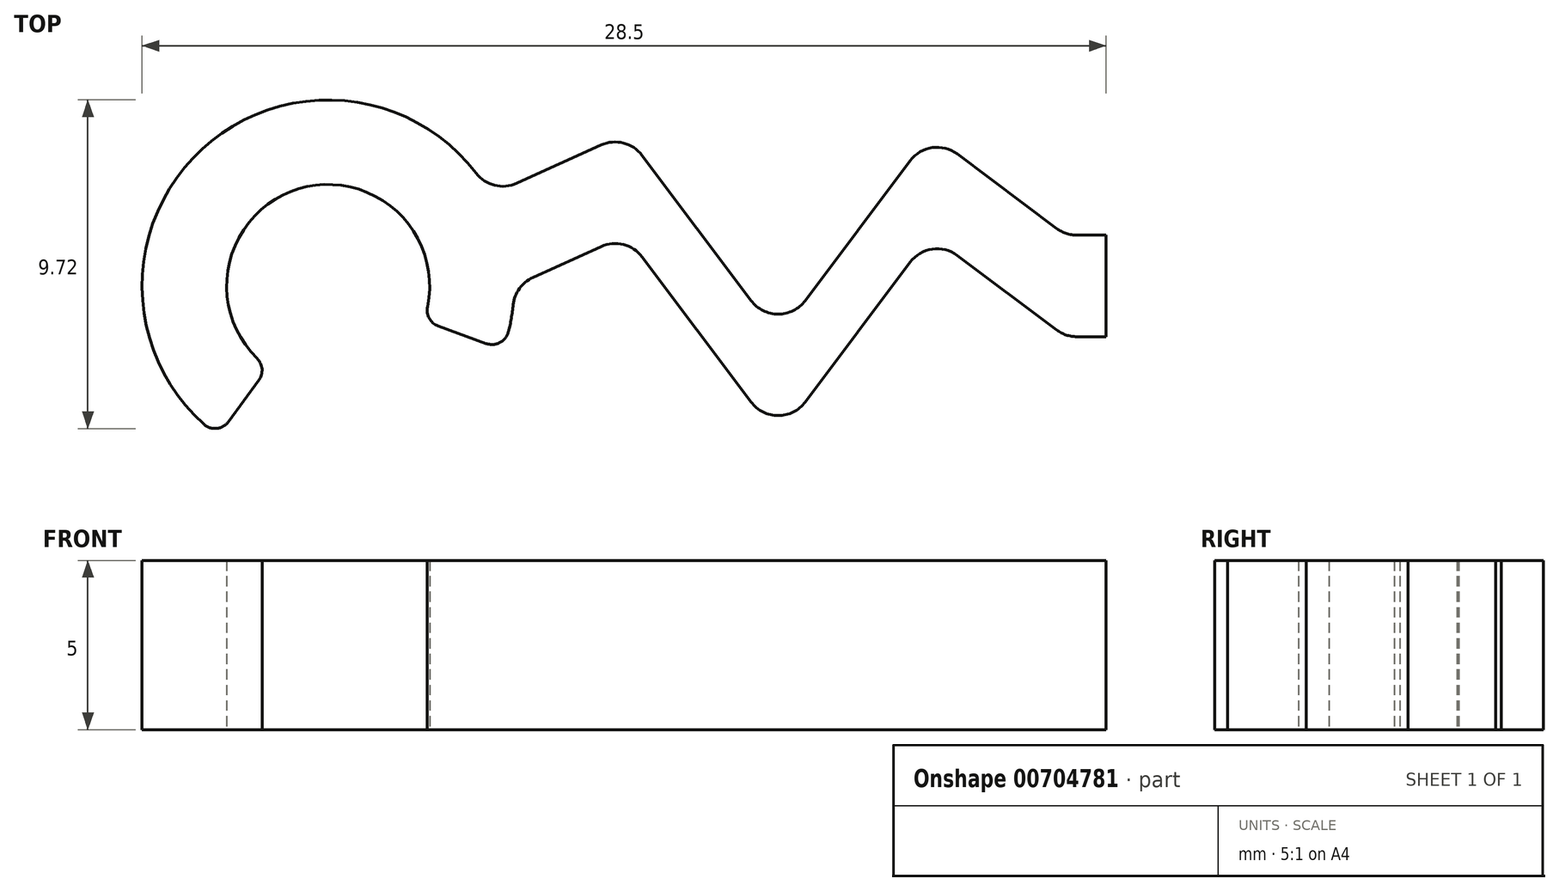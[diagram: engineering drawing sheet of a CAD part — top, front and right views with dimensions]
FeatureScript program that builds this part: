
annotation { "Feature Type Name" : "Feature", "Feature Type Description" : "" }
export const myFeature = defineFeature(function(context is Context, id is Id, definition is map)
    precondition{}
    {
        {
            var Q0;
            Q0=qCreatedBy(makeId("Top.planeOp"),FACE);
            var sketch = newSketch(context, id + "F0", { "sketchPlane" : qUnion([Q0])});
            skArc(sketch, "E0", {"start": v(-20.06, -0.61) * mm, "mid": v(-23.87, 2.87) * mm, "end": v(-25.1, -2.14) * mm});
            skArc(sketch, "E1.0", {"start": v(-17.67, -1.35) * mm, "mid": v(-17.58, -0.96) * mm, "end": v(-17.53, -0.56) * mm});
            skPoint(sketch, "E2", {"position": v(-26, 0) * mm});
            skLineSegment(sketch, "E3", {"start": v(-23, 0) * mm, "end": v(-17.83, -1.88) * mm, "construction": true});
            skLineSegment(sketch, "E4", {"start": v(-23, 0) * mm, "end": v(-26.25, -4.43) * mm, "construction": true});
            skPoint(sketch, "E5", {"position": v(-24.77, -2.42) * mm});
            skPoint(sketch, "E6", {"position": v(-20.18, -1.03) * mm});
            skLineSegment(sketch, "E7", {"start": v(-24.77, -2.42) * mm, "end": v(-20.18, -1.03) * mm, "construction": true});
            skLineSegment(sketch, "E8", {"start": v(-25.05, -2.8) * mm, "end": v(-25.94, -4.01) * mm});
            skLineSegment(sketch, "E9", {"start": v(-19.74, -1.18) * mm, "end": v(-18.33, -1.7) * mm});
            skArc(sketch, "E10.filletArc", {"start": v(-20.06, -0.61) * mm, "mid": v(-20.01, -0.96) * mm, "end": v(-19.74, -1.18) * mm});
            skPoint(sketch, "E11.visualSharp", {"position": v(-17.83, -1.88) * mm});
            skArc(sketch, "E11.filletArc", {"start": v(-18.33, -1.7) * mm, "mid": v(-17.92, -1.67) * mm, "end": v(-17.67, -1.35) * mm});
            skArc(sketch, "E12.filletArc", {"start": v(-25.05, -2.8) * mm, "mid": v(-24.95, -2.46) * mm, "end": v(-25.1, -2.14) * mm});
            skPoint(sketch, "E13.visualSharp", {"position": v(-26.25, -4.43) * mm});
            skArc(sketch, "E13.filletArc", {"start": v(-26.68, -4.09) * mm, "mid": v(-26.3, -4.21) * mm, "end": v(-25.94, -4.01) * mm});
            skLineSegment(sketch, "E14", {"start": v(-26.16, 4.5) * mm, "end": v(0, 4.5) * mm, "construction": true});
            skLineSegment(sketch, "E15.MirrorCS", {"start": v(-26.16, -4.5) * mm, "end": v(0, -4.5) * mm, "construction": true});
            skLineSegment(sketch, "E16", {"start": v(0, 1.5) * mm, "end": v(-26.16, 1.5) * mm, "construction": true});
            skLineSegment(sketch, "E17.MirrorCS", {"start": v(0, -1.5) * mm, "end": v(-26.16, -1.5) * mm, "construction": true});
            skLineSegment(sketch, "E18", {"start": v(-17.42, 3.04) * mm, "end": v(-14.93, 4.17) * mm});
            skLineSegment(sketch, "E19", {"start": v(-13.72, 3.86) * mm, "end": v(-10.5, -0.43) * mm});
            skLineSegment(sketch, "E20", {"start": v(-8.9, -0.43) * mm, "end": v(-5.8, 3.7) * mm});
            skLineSegment(sketch, "E21", {"start": v(-4.4, 3.9) * mm, "end": v(-1.47, 1.7) * mm});
            skLineSegment(sketch, "E22", {"start": v(-1.47, -1.3) * mm, "end": v(-4.4, 0.9) * mm});
            skLineSegment(sketch, "E23", {"start": v(-5.8, 0.7) * mm, "end": v(-8.9, -3.43) * mm});
            skLineSegment(sketch, "E24", {"start": v(-10.5, -3.43) * mm, "end": v(-13.72, 0.86) * mm});
            skLineSegment(sketch, "E25", {"start": v(-14.93, 1.17) * mm, "end": v(-16.95, 0.25) * mm});
            skLineSegment(sketch, "E26", {"start": v(-14.2, 4.5) * mm, "end": v(-14.2, 1.5) * mm, "construction": true});
            skLineSegment(sketch, "E27", {"start": v(-5.2, 1.5) * mm, "end": v(-5.2, 4.5) * mm, "construction": true});
            skLineSegment(sketch, "E28", {"start": v(-9.7, -1.5) * mm, "end": v(-9.7, -4.5) * mm, "construction": true});
            skLineSegment(sketch, "E29", {"start": v(-0.87, 1.5) * mm, "end": v(0, 1.5) * mm});
            skLineSegment(sketch, "E30", {"start": v(0, 1.5) * mm, "end": v(0, -1.5) * mm});
            skLineSegment(sketch, "E31", {"start": v(0, -1.5) * mm, "end": v(-0.87, -1.5) * mm});
            skPoint(sketch, "E32.visualSharp", {"position": v(-14.2, 4.5) * mm});
            skArc(sketch, "E32.filletArc", {"start": v(-13.72, 3.86) * mm, "mid": v(-14.27, 4.23) * mm, "end": v(-14.93, 4.17) * mm});
            skPoint(sketch, "E33.visualSharp", {"position": v(-14.2, 1.5) * mm});
            skArc(sketch, "E33.filletArc", {"start": v(-13.72, 0.86) * mm, "mid": v(-14.27, 1.23) * mm, "end": v(-14.93, 1.17) * mm});
            skPoint(sketch, "E34.visualSharp", {"position": v(-9.7, -4.5) * mm});
            skArc(sketch, "E34.filletArc", {"start": v(-10.5, -3.43) * mm, "mid": v(-9.7, -3.83) * mm, "end": v(-8.9, -3.43) * mm});
            skPoint(sketch, "E35.visualSharp", {"position": v(-9.7, -1.5) * mm});
            skArc(sketch, "E35.filletArc", {"start": v(-10.5, -0.43) * mm, "mid": v(-9.7, -0.83) * mm, "end": v(-8.9, -0.43) * mm});
            skPoint(sketch, "E36.visualSharp", {"position": v(-5.2, 4.5) * mm});
            skArc(sketch, "E36.filletArc", {"start": v(-4.4, 3.9) * mm, "mid": v(-5.14, 4.09) * mm, "end": v(-5.8, 3.7) * mm});
            skPoint(sketch, "E37.visualSharp", {"position": v(-5.2, 1.5) * mm});
            skArc(sketch, "E37.filletArc", {"start": v(-4.4, 0.9) * mm, "mid": v(-5.14, 1.09) * mm, "end": v(-5.8, 0.7) * mm});
            skArc(sketch, "E38.trimOffspring", {"start": v(-18.63, 3.34) * mm, "mid": v(-26.73, 4.04) * mm, "end": v(-26.68, -4.09) * mm});
            skPoint(sketch, "E39.visualSharp", {"position": v(-1.2, 1.5) * mm});
            skArc(sketch, "E39.filletArc", {"start": v(-1.47, 1.7) * mm, "mid": v(-1.18, 1.55) * mm, "end": v(-0.87, 1.5) * mm});
            skPoint(sketch, "E40.visualSharp", {"position": v(-1.2, -1.5) * mm});
            skArc(sketch, "E40.filletArc", {"start": v(-1.47, -1.3) * mm, "mid": v(-1.18, -1.45) * mm, "end": v(-0.87, -1.5) * mm});
            skPoint(sketch, "E41.visualSharp", {"position": v(-18.2, 2.68) * mm});
            skArc(sketch, "E41.filletArc", {"start": v(-18.63, 3.34) * mm, "mid": v(-18.08, 2.98) * mm, "end": v(-17.42, 3.04) * mm});
            skPoint(sketch, "E42.visualSharp", {"position": v(-17.5, 0) * mm});
            skArc(sketch, "E42.filletArc", {"start": v(-16.95, 0.25) * mm, "mid": v(-17.35, -0.08) * mm, "end": v(-17.53, -0.56) * mm});
            skArc(sketch, "E43.MirrorCS", {"start": v(20.06, -0.61) * mm, "mid": v(20.01, -0.96) * mm, "end": v(19.74, -1.18) * mm});
            skArc(sketch, "E44.MirrorCS", {"start": v(25.05, -2.8) * mm, "mid": v(24.95, -2.46) * mm, "end": v(25.1, -2.14) * mm});
            skArc(sketch, "E45.MirrorCS", {"start": v(17.67, -1.35) * mm, "mid": v(17.58, -0.96) * mm, "end": v(17.53, -0.56) * mm});
            skArc(sketch, "E46.MirrorCS", {"start": v(1.47, -1.3) * mm, "mid": v(1.18, -1.45) * mm, "end": v(0.87, -1.5) * mm});
            skArc(sketch, "E47.MirrorCS", {"start": v(13.72, 0.86) * mm, "mid": v(14.27, 1.23) * mm, "end": v(14.93, 1.17) * mm});
            skArc(sketch, "E48.MirrorCS", {"start": v(4.4, 3.9) * mm, "mid": v(5.14, 4.09) * mm, "end": v(5.8, 3.7) * mm});
            skArc(sketch, "E49.MirrorCS", {"start": v(18.33, -1.7) * mm, "mid": v(17.92, -1.67) * mm, "end": v(17.67, -1.35) * mm});
            skArc(sketch, "E50.MirrorCS", {"start": v(1.47, 1.7) * mm, "mid": v(1.18, 1.55) * mm, "end": v(0.87, 1.5) * mm});
            skArc(sketch, "E51.MirrorCS", {"start": v(13.72, 3.86) * mm, "mid": v(14.27, 4.23) * mm, "end": v(14.93, 4.17) * mm});
            skArc(sketch, "E52.MirrorCS", {"start": v(16.95, 0.25) * mm, "mid": v(17.35, -0.08) * mm, "end": v(17.53, -0.56) * mm});
            skArc(sketch, "E53.MirrorCS", {"start": v(26.68, -4.09) * mm, "mid": v(26.3, -4.21) * mm, "end": v(25.94, -4.01) * mm});
            skArc(sketch, "E54.MirrorCS", {"start": v(4.4, 0.9) * mm, "mid": v(5.14, 1.09) * mm, "end": v(5.8, 0.7) * mm});
            skArc(sketch, "E55.MirrorCS", {"start": v(18.63, 3.34) * mm, "mid": v(18.08, 2.98) * mm, "end": v(17.42, 3.04) * mm});
            skPoint(sketch, "E56.MirrorP", {"position": v(24.77, -2.42) * mm});
            skLineSegment(sketch, "E57.MirrorCS", {"start": v(0.87, 1.5) * mm, "end": v(0, 1.5) * mm});
            skLineSegment(sketch, "E58.MirrorCS", {"start": v(0, -1.5) * mm, "end": v(0.87, -1.5) * mm});
            skLineSegment(sketch, "E59.MirrorCS", {"start": v(25.05, -2.8) * mm, "end": v(25.94, -4.01) * mm});
            skPoint(sketch, "E60.MirrorP", {"position": v(20.18, -1.03) * mm});
            skLineSegment(sketch, "E61.MirrorCS", {"start": v(19.74, -1.18) * mm, "end": v(18.33, -1.7) * mm});
            skPoint(sketch, "E62.MirrorP", {"position": v(9.7, -1.5) * mm});
            skLineSegment(sketch, "E63.MirrorCS", {"start": v(4.4, 3.9) * mm, "end": v(1.47, 1.7) * mm});
            skArc(sketch, "E64.MirrorCS", {"start": v(10.5, -3.43) * mm, "mid": v(9.7, -3.83) * mm, "end": v(8.9, -3.43) * mm});
            skLineSegment(sketch, "E65.MirrorCS", {"start": v(1.47, -1.3) * mm, "end": v(4.4, 0.9) * mm});
            skLineSegment(sketch, "E66.MirrorCS", {"start": v(0, -1.5) * mm, "end": v(26.16, -1.5) * mm, "construction": true});
            skLineSegment(sketch, "E67.MirrorCS", {"start": v(17.42, 3.04) * mm, "end": v(14.93, 4.17) * mm});
            skPoint(sketch, "E68.MirrorP", {"position": v(1.2, 1.5) * mm});
            skLineSegment(sketch, "E69.MirrorCS", {"start": v(9.7, -1.5) * mm, "end": v(9.7, -4.5) * mm, "construction": true});
            skArc(sketch, "E70.MirrorCS", {"start": v(20.06, -0.61) * mm, "mid": v(23.87, 2.87) * mm, "end": v(25.1, -2.14) * mm});
            skPoint(sketch, "E71.MirrorP", {"position": v(26, 0) * mm});
            skLineSegment(sketch, "E72.MirrorCS", {"start": v(23, 0) * mm, "end": v(17.83, -1.88) * mm, "construction": true});
            skPoint(sketch, "E73.MirrorP", {"position": v(14.2, 1.5) * mm});
            skLineSegment(sketch, "E74.MirrorCS", {"start": v(5.8, 0.7) * mm, "end": v(8.9, -3.43) * mm});
            skPoint(sketch, "E75.MirrorP", {"position": v(1.2, -1.5) * mm});
            skLineSegment(sketch, "E76.MirrorCS", {"start": v(5.2, 1.5) * mm, "end": v(5.2, 4.5) * mm, "construction": true});
            skLineSegment(sketch, "E77.MirrorCS", {"start": v(10.5, -3.43) * mm, "end": v(13.72, 0.86) * mm});
            skPoint(sketch, "E78.MirrorP", {"position": v(9.7, -4.5) * mm});
            skPoint(sketch, "E79.MirrorP", {"position": v(17.5, 0) * mm});
            skPoint(sketch, "E80.MirrorP", {"position": v(26.25, -4.43) * mm});
            skLineSegment(sketch, "E81.MirrorCS", {"start": v(24.77, -2.42) * mm, "end": v(20.18, -1.03) * mm, "construction": true});
            skLineSegment(sketch, "E82.MirrorCS", {"start": v(13.72, 3.86) * mm, "end": v(10.5, -0.43) * mm});
            skLineSegment(sketch, "E83.MirrorCS", {"start": v(23, 0) * mm, "end": v(26.25, -4.43) * mm, "construction": true});
            skPoint(sketch, "E84.MirrorP", {"position": v(17.83, -1.88) * mm});
            skPoint(sketch, "E85.MirrorP", {"position": v(5.2, 1.5) * mm});
            skPoint(sketch, "E86.MirrorP", {"position": v(18.2, 2.68) * mm});
            skArc(sketch, "E87.MirrorCS", {"start": v(10.5, -0.43) * mm, "mid": v(9.7, -0.83) * mm, "end": v(8.9, -0.43) * mm});
            skArc(sketch, "E88.MirrorCS", {"start": v(18.63, 3.34) * mm, "mid": v(26.73, 4.04) * mm, "end": v(26.68, -4.09) * mm});
            skLineSegment(sketch, "E89.MirrorCS", {"start": v(0, 1.5) * mm, "end": v(26.16, 1.5) * mm, "construction": true});
            skLineSegment(sketch, "E90.MirrorCS", {"start": v(26.16, 4.5) * mm, "end": v(0, 4.5) * mm, "construction": true});
            skPoint(sketch, "E91.MirrorP", {"position": v(5.2, 4.5) * mm});
            skLineSegment(sketch, "E92.MirrorCS", {"start": v(14.93, 1.17) * mm, "end": v(16.95, 0.25) * mm});
            skLineSegment(sketch, "E93.MirrorCS", {"start": v(14.2, 4.5) * mm, "end": v(14.2, 1.5) * mm, "construction": true});
            skPoint(sketch, "E94.MirrorP", {"position": v(14.2, 4.5) * mm});
            skLineSegment(sketch, "E95.MirrorCS", {"start": v(8.9, -0.43) * mm, "end": v(5.8, 3.7) * mm});
            skLineSegment(sketch, "E96.MirrorCS", {"start": v(26.16, -4.5) * mm, "end": v(0, -4.5) * mm, "construction": true});
            skSolve(sketch);
        }
        {
            var Q0;
            Q0=makeQuery(id+"F0.imprint","IMPRINT",FACE,{"disambiguationData":[TD([[makeQuery(id+"F0.imprint","IMPRINT",EDGE,{"derivedFrom":sQuery(id+"F0.wireOp",EDGE,"E0")}),-1.0]])]});
            var Q1;
            Q1=makeQuery(id+"F0.imprint","IMPRINT",FACE,{"disambiguationData":[TD([[makeQuery(id+"F0.imprint","IMPRINT",EDGE,{"derivedFrom":sQuery(id+"F0.wireOp",EDGE,"E43.MirrorCS")}),-1.0]])]});
            extrude(context, id + "F1", {"entities" : qUnion([Q0, Q1]), "depth" : 5 * mm, "offsetDistance" : 25 * mm});
        }
    });
